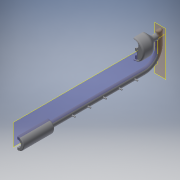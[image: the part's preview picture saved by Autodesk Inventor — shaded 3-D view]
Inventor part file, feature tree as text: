
AUTODESK INVENTOR PART (.ipt)
format: ipt  version: 2018 (Build 220112000, 112)  size: 369,152 bytes
history: native  units: mm
features: sketch x11, extrude x7, projected_geometry x7, fillet x5, plane x3, revolve x2, sweep x1
ambient origin geometry x8: Origin, YZ Plane, XZ Plane, XY Plane, X Axis, Y Axis, Z Axis, Center Point
bodies: Solid1 (feature_tree)
feature tree (36):
  revolve  "Revolution1"  [1 undecoded]
  fillet  "Fillet1"  Radius=40.0mm
  fillet  "Fillet2"  [1 undecoded]
  sweep  "Sweep2"
  plane  "Work Plane6"
  revolve  "Revolution4"  [1 undecoded]
  extrude  "Extrusion10"  Depth=2.0mm
  extrude  "Extrusion11"  Depth=20.0mm TaperAngle=0.0deg
  extrude  "Extrusion15"  Depth=8.25mm
  extrude  "Extrusion4"  Depth=5.0mm
  fillet  "Fillet7"  Radius=1.5mm
  plane  "Work Plane7"
  extrude  "Extrusion12"  Depth=20.0mm
  extrude  "Extrusion13"  TaperAngle=0.0deg  [1 undecoded]
  fillet  "Fillet8"  [1 undecoded]
  plane  "Work Plane8"
  extrude  "Extrusion14"  Depth=9.0mm
  fillet  "Fillet9"  Radius=9.0mm
  sketch  "Sketch1"  dims[d0=160.0mm d3=8.0mm d4=40.0mm d5=90.0deg]
  sketch  "Sketch11"  dims[d20=1.5mm d22=1.5mm]
  sketch  "Sketch17"  dims[d26=1.5mm d27=4.0mm]
  sketch  "Sketch18"  dims[d29=9.0mm d30=2.0mm]
  projected_geometry  "Projected Loop6"
  sketch  "Sketch19"  dims[d31=1.0mm d55=20.0mm d56=0.0mm]
  sketch  "Sketch20"  dims[d73=8.25mm d74=8.25mm]
  projected_geometry  "Projected Loop7"
  sketch  "Sketch21"  dims[d75=0.0mm d78=5.0mm d79=1.5mm]
  projected_geometry  "Projected Loop8"
  sketch  "Sketch22"  dims[d80=20.0mm d81=20.0mm]
  projected_geometry  "Projected Loop9"
  sketch  "Sketch23"  dims[d82=15.0mm d83=0.0mm d84=0.0mm d85=-5.0mm]
  projected_geometry  "Projected Loop10"
  sketch  "Sketch24"  dims[d87=9.822747mm d88=9.0mm d89=9.0mm]
  projected_geometry  "Projected Loop11"
  sketch  "Sketch25"  dims[d90=9.0mm d91=90.0deg d92=2.0mm d93=0.0mm d94=5.0mm d95=5.0mm d96=5.5mm d97=9.0mm d98=2.0mm d99=0.0mm d101=5.0mm d102=4.0mm d103=0.0mm d104=10.0mm d105=0.0mm d106=1.0mm d107=-3.0mm d109=1.8mm d110=14.0mm d111=50.0mm d113=20.0mm d114=10.0mm d116=10.0mm d118=5.0mm d119=0.0mm d120=0.5mm d121=2.0mm d122=1.5mm d123=2.0mm d124=0.0mm d125=2.0mm]
  projected_geometry  "Projected Loop12"
note: 5 required parameter values undecoded (feature->parameter linkage not recoverable at this tier; creation-order binding heuristic only, values carry confidence <= 0.55)